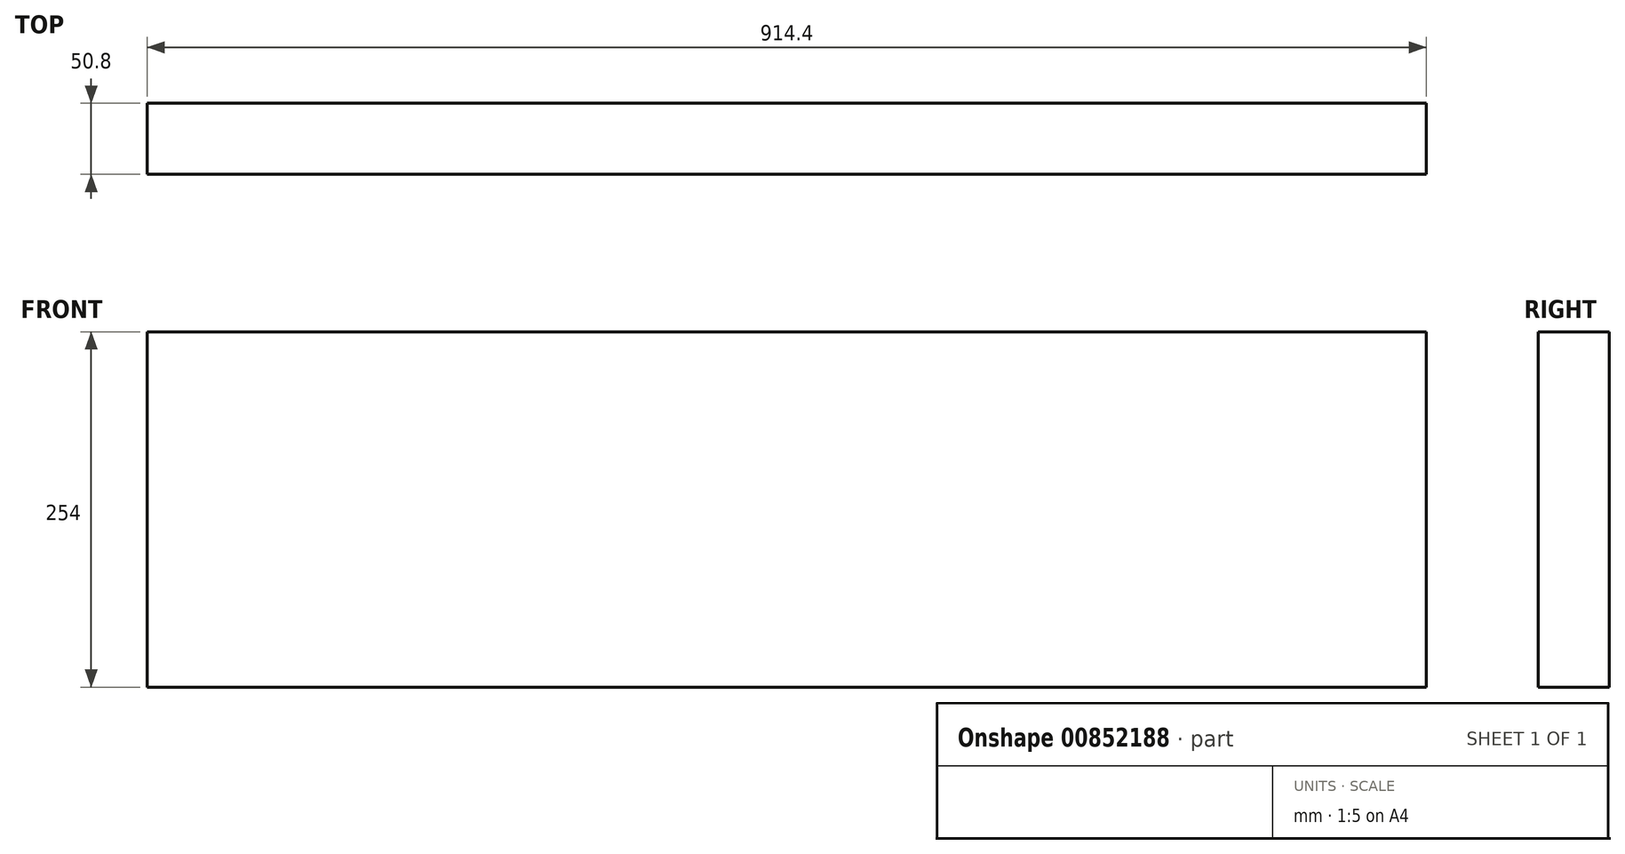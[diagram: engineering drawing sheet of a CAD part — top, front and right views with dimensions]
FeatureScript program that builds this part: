
annotation { "Feature Type Name" : "Feature", "Feature Type Description" : "" }
export const myFeature = defineFeature(function(context is Context, id is Id, definition is map)
    precondition{}
    {
        {
            var Q0;
            Q0=qCreatedBy(makeId("Top.planeOp"),FACE);
            var sketch = newSketch(context, id + "F0", { "sketchPlane" : qUnion([Q0])});
            skLineSegment(sketch, "E0.bottom", {"start": v(457.2, 25.4) * mm, "end": v(-457.2, 25.4) * mm});
            skLineSegment(sketch, "E0.top", {"start": v(457.2, -25.4) * mm, "end": v(-457.2, -25.4) * mm});
            skLineSegment(sketch, "E0.left", {"start": v(457.2, 25.4) * mm, "end": v(457.2, -25.4) * mm});
            skLineSegment(sketch, "E0.right", {"start": v(-457.2, 25.4) * mm, "end": v(-457.2, -25.4) * mm});
            skPoint(sketch, "E0.middle", {"position": v(0, 0) * mm});
            skSolve(sketch);
        }
        {
            var Q0;
            Q0 = qSketchRegion(id + "F0", true);
            extrude(context, id + "F1", {"entities" : qUnion([Q0]), "depth" : 254 * mm, "offsetDistance" : 25.4 * mm});
        }
    });
